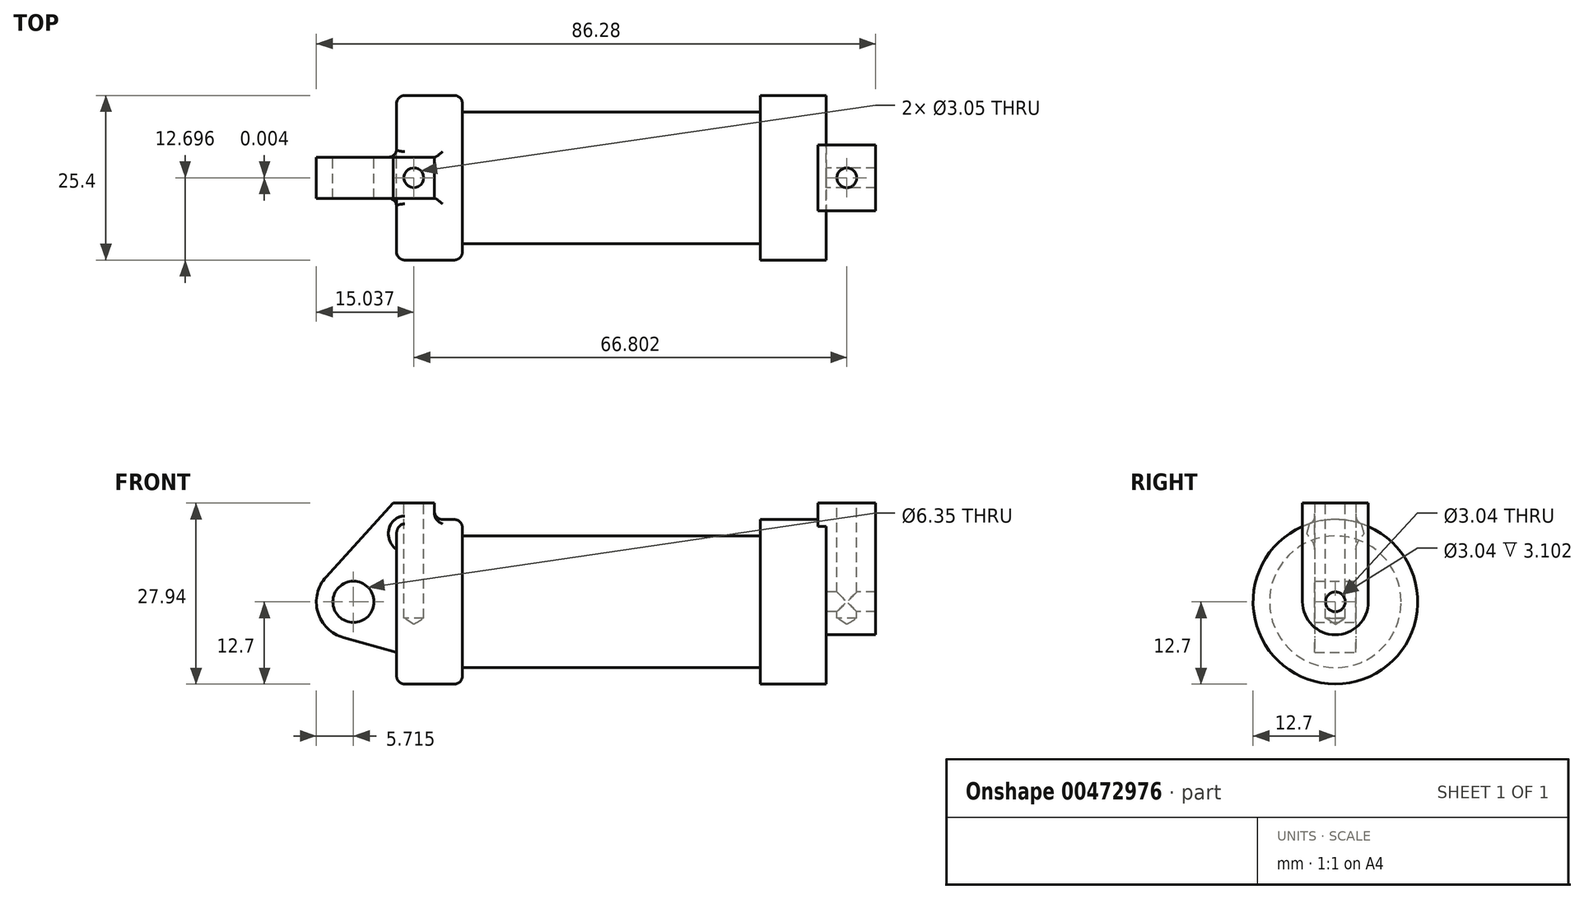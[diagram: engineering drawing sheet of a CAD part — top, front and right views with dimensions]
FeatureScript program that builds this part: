
annotation { "Feature Type Name" : "Feature", "Feature Type Description" : "" }
export const myFeature = defineFeature(function(context is Context, id is Id, definition is map)
    precondition{}
    {
        {
            var Q0;
            Q0=qCreatedBy(makeId("Front.planeOp"),FACE);
            var sketch = newSketch(context, id + "F0", { "sketchPlane" : qUnion([Q0])});
            skLineSegment(sketch, "E0", {"start": v(0, 0) * mm, "end": v(0, 12.7) * mm});
            skLineSegment(sketch, "E1", {"start": v(0, 12.7) * mm, "end": v(10.16, 12.7) * mm});
            skLineSegment(sketch, "E2", {"start": v(10.16, 12.7) * mm, "end": v(10.16, 10.16) * mm});
            skLineSegment(sketch, "E3", {"start": v(10.16, 10.16) * mm, "end": v(56.13, 10.16) * mm});
            skLineSegment(sketch, "E4", {"start": v(56.13, 10.16) * mm, "end": v(56.13, 12.7) * mm});
            skLineSegment(sketch, "E5", {"start": v(56.13, 12.7) * mm, "end": v(66.3, 12.7) * mm});
            skLineSegment(sketch, "E6", {"start": v(66.3, 12.7) * mm, "end": v(66.3, 0) * mm});
            skLineSegment(sketch, "E7", {"start": v(66.3, 0) * mm, "end": v(0, 0) * mm});
            skLineSegment(sketch, "E8", {"start": v(5.84, 15.24) * mm, "end": v(-0.5, 15.24) * mm});
            skLineSegment(sketch, "E9", {"start": v(-0.5, 15.24) * mm, "end": v(-10.88, 3.85) * mm});
            skLineSegment(sketch, "E10", {"start": v(0, 0) * mm, "end": v(-6.65, 0) * mm});
            skCircle(sketch, "E11", {"center": v(-6.65, 0) * mm, "radius": 5.72 * mm});
            skCircle(sketch, "E12", {"center": v(-6.65, 0) * mm, "radius": 3.18 * mm});
            skLineSegment(sketch, "E13", {"start": v(5.84, 15.24) * mm, "end": v(5.84, -9.4) * mm});
            skLineSegment(sketch, "E14", {"start": v(5.84, -9.4) * mm, "end": v(-8.18, -5.5) * mm});
            skSolve(sketch);
        }
        {
            var Q0;
            {var subQ0=sQuery(id+"F0.wireOp",EDGE,"E2");Q0=makeQuery(id+"F0.imprint","IMPRINT",FACE,{"disambiguationData":[TD([[makeQuery(id+"F0.imprint","IMPRINT",EDGE,{"derivedFrom":subQ0}),-1.0]])]});}
            var Q1;
            {var subQ0=sQuery(id+"F0.wireOp",EDGE,"E0");Q1=makeQuery(id+"F0.imprint","IMPRINT",FACE,{"disambiguationData":[TD([[makeQuery(id+"F0.imprint","IMPRINT",EDGE,{"derivedFrom":subQ0}),-1.0]])]});}
            var Q2;
            Q2=sQuery(id+"F0.wireOp",EDGE,"E7");
            revolve(context, id + "F1", {"entities" : qUnion([Q0, Q1]), "axis" : qUnion([Q2]), "revolveType" : RevolveType.FULL});
        }
        {
            var Q0;
            {var subQ1=sQuery(id+"F0.wireOp",EDGE,"E0");Q0=makeQuery(id+"F0.imprint","IMPRINT",FACE,{"disambiguationData":[TD([[makeQuery(id+"F0.imprint","IMPRINT",EDGE,{"derivedFrom":subQ1}),1.0]])]});}
            var Q1;
            {var subQ0=sQuery(id+"F0.wireOp",EDGE,"E14");Q1=makeQuery(id+"F0.imprint","IMPRINT",FACE,{"disambiguationData":[TD([[makeQuery(id+"F0.imprint","IMPRINT",EDGE,{"derivedFrom":subQ0}),-1.0]])]});}
            var Q2;
            {var subQ5=sQuery(id+"F0.wireOp",EDGE,"E12");Q2=makeQuery(id+"F0.imprint","IMPRINT",FACE,{"disambiguationData":[TD([[makeQuery(id+"F0.imprint","IMPRINT",EDGE,{"derivedFrom":subQ5}),-1.0]])]});}
            var Q3;
            {var subQ0=sQuery(id+"F0.wireOp",EDGE,"E0");Q3=makeQuery(id+"F0.imprint","IMPRINT",FACE,{"disambiguationData":[TD([[makeQuery(id+"F0.imprint","IMPRINT",EDGE,{"derivedFrom":subQ0}),-1.0]])]});}
            extrude(context, id + "F2", {"entities" : qUnion([Q0, Q1, Q2, Q3]), "operationType" : NewBodyOperationType.ADD, "endBound" : BoundingType.SYMMETRIC, "depth" : 6.35 * mm, "offsetDistance" : 25.4 * mm});
        }
        {
            var Q0;
            Q0=makeQuery(id+"F1.opRevolve","SWEPT_FACE",FACE,{"disambiguationData":[OSD([sQuery(id+"F0.wireOp",EDGE,"E6")])]});
            var sketch = newSketch(context, id + "F3", { "sketchPlane" : qUnion([Q0])});
            skCircle(sketch, "E15", {"center": v(0, 0) * mm, "radius": 1.52 * mm});
            skCircle(sketch, "E16", {"center": v(0, 0) * mm, "radius": 5.08 * mm});
            skLineSegment(sketch, "E17", {"start": v(0, 0) * mm, "end": v(0, 15.24) * mm});
            skLineSegment(sketch, "E18", {"start": v(-5.08, 0) * mm, "end": v(-5.08, 15.24) * mm});
            skLineSegment(sketch, "E19", {"start": v(-5.08, 15.24) * mm, "end": v(5.07, 15.24) * mm});
            skLineSegment(sketch, "E20", {"start": v(5.07, 15.24) * mm, "end": v(5.08, 0) * mm});
            skLineSegment(sketch, "E21", {"start": v(0, 0) * mm, "end": v(0, -1.52) * mm});
            skLineSegment(sketch, "E22", {"start": v(0, 0) * mm, "end": v(-1.52, 0) * mm});
            skLineSegment(sketch, "E23", {"start": v(0, 0) * mm, "end": v(1.52, 0) * mm});
            skSolve(sketch);
        }
        {
            var Q0;
            {var subQ0=sQuery(id+"F3.wireOp",EDGE,"E19");var subQ5=sQuery(id+"F3.wireOp",EDGE,"E20");var subQ6=makeQuery(id+"F3.imprint","INTERSECT",VERTEX,{"derivedFrom":[subQ0,subQ5]});Q0=makeQuery(id+"F3.imprint","IMPRINT",FACE,{"disambiguationData":[TD([[makeQuery(id+"F3.imprint","IMPRINT",EDGE,{"disambiguationData":[TD([[subQ6,1.0]])],"derivedFrom":subQ0}),-1.0]])]});}
            var Q1;
            {var subQ0=sQuery(id+"F3.wireOp",EDGE,"E19");var subQ5=sQuery(id+"F3.wireOp",EDGE,"E18");var subQ6=makeQuery(id+"F3.imprint","INTERSECT",VERTEX,{"derivedFrom":[subQ5,subQ0]});Q1=makeQuery(id+"F3.imprint","IMPRINT",FACE,{"disambiguationData":[TD([[makeQuery(id+"F3.imprint","IMPRINT",EDGE,{"disambiguationData":[TD([[subQ6,-1.0]])],"derivedFrom":subQ0}),-1.0]])]});}
            var Q2;
            {var subQ0=sQuery(id+"F3.wireOp",EDGE,"E18");var subQ1=sQuery(id+"F3.wireOp",EDGE,"E16");var subQ2=makeQuery(id+"F3.imprint","INTERSECT",VERTEX,{"derivedFrom":[subQ1,subQ0]});Q2=makeQuery(id+"F3.imprint","IMPRINT",FACE,{"disambiguationData":[TD([[makeQuery(id+"F3.imprint","IMPRINT",EDGE,{"disambiguationData":[TD([[subQ2,1.0]])],"derivedFrom":subQ1}),-1.0]])]});}
            var Q3;
            {var subQ0=sQuery(id+"F3.wireOp",EDGE,"E20");var subQ1=sQuery(id+"F3.wireOp",EDGE,"E16");var subQ2=makeQuery(id+"F3.imprint","INTERSECT",VERTEX,{"derivedFrom":[subQ1,subQ0]});Q3=makeQuery(id+"F3.imprint","IMPRINT",FACE,{"disambiguationData":[TD([[makeQuery(id+"F3.imprint","IMPRINT",EDGE,{"disambiguationData":[TD([[subQ2,-1.0]])],"derivedFrom":subQ1}),-1.0]])]});}
            var Q4;
            Q4=makeQuery(id+"F3.imprint","IMPRINT",FACE,{"disambiguationData":[TD([[makeQuery(id+"F3.imprint","IMPRINT",EDGE,{"derivedFrom":sQuery(id+"F3.wireOp",EDGE,"E15")}),-1.0]])]});
            extrude(context, id + "F4", {"entities" : qUnion([Q0, Q1, Q2, Q3, Q4]), "operationType" : NewBodyOperationType.ADD, "depth" : 7.62 * mm, "hasSecondDirection" : true, "secondDirectionOppositeDirection" : true, "secondDirectionDepth" : 1.27 * mm});
        }
        {
            var Q0;
            Q0=makeQuery(id+"F4.opExtrude","SWEPT_FACE",FACE,{"disambiguationData":[OSD([sQuery(id+"F3.wireOp",EDGE,"E19")])]});
            var sketch = newSketch(context, id + "F5", { "sketchPlane" : qUnion([Q0])});
            skCircle(sketch, "E24", {"center": v(2.67, 0) * mm, "radius": 1.52 * mm});
            skSolve(sketch);
        }
        {
            var Q0;
            Q0=sQuery(id+"F5.wireOp",VERTEX,"E24.center");
            var Q1;
            Q1=makeQuery(id+"F1.opRevolve","SWEPT_BODY",BODY,{"disambiguationData":[OSD([sQuery(id+"F0.wireOp",EDGE,"E0"),sQuery(id+"F0.wireOp",EDGE,"E1"),sQuery(id+"F0.wireOp",EDGE,"E2"),sQuery(id+"F0.wireOp",EDGE,"E3"),sQuery(id+"F0.wireOp",EDGE,"E4"),sQuery(id+"F0.wireOp",EDGE,"E5"),sQuery(id+"F0.wireOp",EDGE,"E6"),sQuery(id+"F0.wireOp",EDGE,"E7")])]});
            hole(context, id + "F6", {"style" : HoleStyle.SIMPLE, "endStyle" : HoleEndStyle.BLIND, "holeDiameter" : 3.05 * mm, "holeDepth" : 17.78 * mm, "isTappedThrough" : true, "tappedDepth" : 12.7 * mm, "tapClearance" : 3, "locations" : qUnion([Q0]), "scope" : qUnion([Q1])});
        }
        {
            var Q0;
            Q0=makeQuery(id+"F4.opExtrude","SWEPT_FACE",FACE,{"disambiguationData":[OSD([sQuery(id+"F3.wireOp",EDGE,"E19")])]});
            var sketch = newSketch(context, id + "F7", { "sketchPlane" : qUnion([Q0])});
            skCircle(sketch, "E25", {"center": v(69.47, 0) * mm, "radius": 1.52 * mm});
            skSolve(sketch);
        }
        {
            var Q0;
            Q0=sQuery(id+"F7.wireOp",VERTEX,"E25.center");
            var Q1;
            Q1=makeQuery(id+"F1.opRevolve","SWEPT_BODY",BODY,{"disambiguationData":[OSD([sQuery(id+"F0.wireOp",EDGE,"E0"),sQuery(id+"F0.wireOp",EDGE,"E1"),sQuery(id+"F0.wireOp",EDGE,"E2"),sQuery(id+"F0.wireOp",EDGE,"E3"),sQuery(id+"F0.wireOp",EDGE,"E4"),sQuery(id+"F0.wireOp",EDGE,"E5"),sQuery(id+"F0.wireOp",EDGE,"E6"),sQuery(id+"F0.wireOp",EDGE,"E7")])]});
            hole(context, id + "F8", {"style" : HoleStyle.SIMPLE, "endStyle" : HoleEndStyle.BLIND, "holeDiameter" : 3.05 * mm, "holeDepth" : 17.78 * mm, "isTappedThrough" : true, "tappedDepth" : 12.7 * mm, "tapClearance" : 3, "locations" : qUnion([Q0]), "scope" : qUnion([Q1])});
        }
        {
            var Q0;
            Q0=makeQuery(id+"F1.opRevolve","SWEPT_FACE",FACE,{"disambiguationData":[OSD([sQuery(id+"F0.wireOp",EDGE,"E1")])]});
            fillet(context, id + "F9", {"entities" : qUnion([Q0]), "radius" : 1.27 * mm, "tangentPropagation" : true, "allowEdgeOverflow" : false});
        }
    });
